# Revit family: SinkMixer_Countertop_Vitra_XLineSeries_A42115
name_source: partatom
category: Plumbing Fixtures
revit_build: Autodesk Revit 2017 (Build: 20160225_1515(x64)
units: mm (PartAtom-declared; Revit-internal decimal feet)

## family parameters
Cut with Voids When Loaded = No
Host = Face
OmniClass Number = 23.45.55.17
OmniClass Title = Mixing Faucets
Part Type = Normal
Room Calculation Point = No
Round Connector Dimension = Use Diameter
Shared = Yes

## types (10) — shared parameters
BIMobject category = Taps & Mixers
CW Connection = Yes
Default Elevation = 850 mm  [stored 2.78871 ft]
Depth(mm) = 185 mm  [stored 0.606955 ft]
Description = X-Line Sink Mixer
Design country = Turkey
HW Connection = Yes
Height(mm) = 393 mm  [stored 1.28937 ft]
Hot Water Supply (max.) = 80 °C
Hot Water temperature, factory set to = 38 °C
IFC Classification = Sanitary Terminal
Main Material = Brass
Manufacturer = Vitra
Manufacturer name = Vitra
Masterformat 2014 Code = 22 40 00
Masterformat 2014 Description = Plumbing Fixtures
Min. flow pressure of = 0.5 bar
MountingType = Countertop
NBS Referans Code = 45-35-70/371
NBS Referans Description = Water supply fittings for wash basins and troughs
Nominal height = 0.000
Nominal width = 0.000
Number Of Connections = 2 mm  [stored 0.00656168 ft]
OmniClass Code = 23.45.55.17
OmniClass Description = Mixing Faucets
Product Properties = Extra Water Saving,Green Building Certification,Energy Saving
Product certification = https://vitraglobal.com
Product family = X-Line
Range of Hot Water Supply = 5 - 65 °C
Range of flow pressure = 1 - 5 bar
Test Pressure = 16 bar
UNSPSC Code = 301815
Uniclass 1.4 Code = L725111
Uniclass 1.4 Description = Mixer taps
Uniclass 2.0 Code = Pr_40_30_96_98
Uniclass 2.0 Description = Washbasin Tap
Uniclass 2015 Code = Pr_40_20_87_98
Uniclass 2015 Name = Washbasin Tap
Uniformat II Code = 22 40 00
Uniformat II Description = Plumbing Fixture
Weight Net (kg) = 1.665
Width(mm) = 149 mm  [stored 0.488845 ft]
Youtube = https://www.youtube.com
zero-valued in all types: Cost

## per-type parameters (varying)
| type | Article No. (default) | Brand | Coating Material | Color | Connection Diameter (mm) | Installation instructions | Model | Product Guid | Product SKU | Product Type | Product data url | Product group | Product url | Technical description | URL | Warranty Period (Year) |
| SinkMixer-XLineSeries(Chrome)-A42115 | A42115 | Artema | Chrome | Chrome | 10 mm  [stored 0.0328084 ft] |  | A42115 |  | A42115 | Sink Mixer |  | X-Line Sink Mixer | https://www.vitra.com.tr | https://www.vitra.com.tr | https://www.vitra.com.tr | 10 Years |
| SinkMixer-XLineSeries(Gold)-A4211523 | A4211523 | Artema | Gold | Gold | 10 mm  [stored 0.0328084 ft] |  | A4211523 |  | A4211523 | Basin Mixer | https://www.vitra.com.tr | X-Line Basin Mixer |  | https://www.vitra.com.tr | https://www.vitra.com.tr | 10 Years |
| SinkMixer-XLineSeries(Chrome)-A42115EXP | A42115EXP | Vitra | Chrome | Chrome | 10 mm  [stored 0.0328084 ft] | https://cdn.vitra.com.tr | A42115EXP | https://cdn.vitra.com.tr | A42115EXP | Basin Mixer | https://www.vitraglobal.com | X-Line Basin Mixer |  | https://www.vitraglobal.com | https://www.vitraglobal.com | 7 Years |
| SinkMixer-XLineSeries(Gold)-A4211523EXP | A4211523EXP | Vitra | Gold | Gold | 10 mm  [stored 0.0328084 ft] | https://cdn.vitra.com.tr | A4211523EXP | https://cdn.vitra.com.tr | A4211523EXP | Basin Mixer | https://www.vitraglobal.com | X-Line Basin Mixer |  | https://www.vitraglobal.com | https://www.vitraglobal.com | 7 Years |
| SinkMixer-XLineSeries(Gold)-A4211523IND | A4211523IND | Vitra | Gold | Gold | 15 mm  [stored 0.0492126 ft] | https://cdn.vitra.com.tr | A4211523IND | https://cdn.vitra.com.tr | A4211523IND | Basin Mixer | https://www.vitraglobal.com | X-Line Basin Mixer |  | https://www.vitraglobal.com | https://www.vitraglobal.com | 7 Years |
| SinkMixer-XLineSeries(Chrome)-A42115IND | A42115IND | Vitra | Chrome | Chrome | 15 mm  [stored 0.0492126 ft] | https://cdn.vitra.com.tr | A42115IND | https://cdn.vitra.com.tr | A42115IND | Basin Mixer | https://www.vitraglobal.com | X-Line Basin Mixer |  | https://www.vitraglobal.com | https://www.vitraglobal.com | 7 Years |
| SinkMixer-XLineSeries(Chrome)-A42115VUK | A42115VUK | Vitra | Chrome | Chrome | 15 mm  [stored 0.0492126 ft] | https://cdn.vitra.com.tr | A42115VUK | https://cdn.vitra.com.tr | A42115VUK | Basin Mixer | https://www.vitraglobal.com | X-Line Basin Mixer |  | https://www.vitraglobal.com | https://www.vitraglobal.com | 7 Years |
| SinkMixer-XLineSeries(Chrome)-A42115ENG | A42115ENG | Vitra | Chrome | Chrome | 10 mm  [stored 0.0328084 ft] | https://cdn.vitra.com.tr | A42115ENG | https://cdn.vitra.com.tr | A42115ENG | Basin Mixer | https://www.vitraglobal.com | X-Line Basin Mixer |  | https://www.vitraglobal.com | https://www.vitraglobal.com | 7 Years |
| SinkMixer-XLineSeries(Chrome)-A42115EKM | A42115EKM | Vitra | Chrome | Chrome | 10 mm  [stored 0.0328084 ft] | https://cdn.vitra.com.tr | A42115EKM | https://cdn.vitra.com.tr | A42115EKM | Basin Mixer | https://www.vitraglobal.com | X-Line Basin Mixer |  | https://www.vitraglobal.com | https://www.vitraglobal.com | 7 Years |
| SinkMixer-XLineSeries(Chrome)-A42115EKF | A42115EKF | Vitra | Chrome | Chrome | 10 mm  [stored 0.0328084 ft] | https://cdn.vitra.com.tr | A42115EKF | https://cdn.vitra.com.tr | A42115EKF | Basin Mixer | https://www.vitraglobal.com | X-Line Basin Mixer |  | https://www.vitraglobal.com | https://www.vitraglobal.com | 7 Years |

note: [stored X ft] marks values corroborated as IEEE doubles in the binary element streams (Revit-internal decimal feet)

## geometry (parser evidence)
native form markers: Sweep x3
no freeform markers — native parametric forms only
